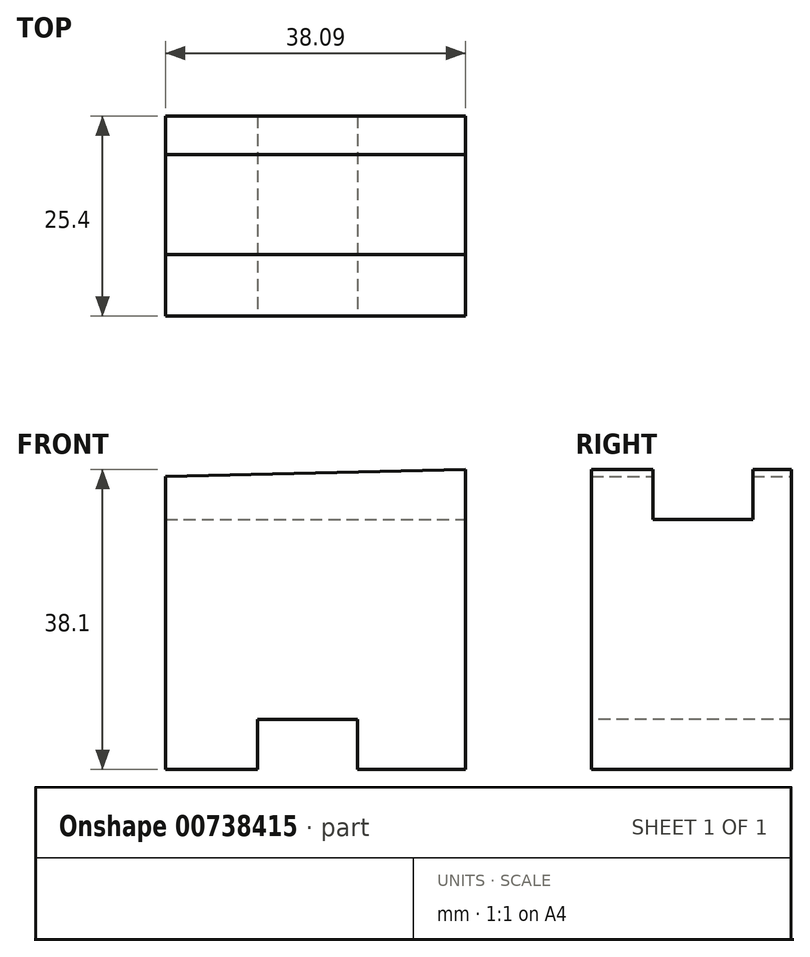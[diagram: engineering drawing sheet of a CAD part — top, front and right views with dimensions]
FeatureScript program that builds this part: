
annotation { "Feature Type Name" : "Feature", "Feature Type Description" : "" }
export const myFeature = defineFeature(function(context is Context, id is Id, definition is map)
    precondition{}
    {
        {
            var Q0;
            Q0=qCreatedBy(makeId("Front.planeOp"),FACE);
            var sketch = newSketch(context, id + "F0", { "sketchPlane" : qUnion([Q0])});
            skLineSegment(sketch, "E0", {"start": v(0, 38.1) * mm, "end": v(0, 0) * mm});
            skLineSegment(sketch, "E1", {"start": v(-0.01, 0.91) * mm, "end": v(38.09, 0.91) * mm});
            skLineSegment(sketch, "E2", {"start": v(38.09, 0.91) * mm, "end": v(38.09, 39.01) * mm});
            skLineSegment(sketch, "E3", {"start": v(38.09, 39.01) * mm, "end": v(0, 38.1) * mm});
            skSolve(sketch);
        }
        {
            var Q0;
            Q0 = qSketchRegion(id + "F0", true);
            extrude(context, id + "F1", {"entities" : qUnion([Q0]), "depth" : 25.4 * mm, "offsetDistance" : 25.4 * mm});
        }
        {
            var Q0;
            Q0=makeQuery(id+"F1.opExtrude","CAP_FACE",FACE,{"disambiguationData":[OSD([sQuery(id+"F0.wireOp",EDGE,"E0"),sQuery(id+"F0.wireOp",EDGE,"E1"),sQuery(id+"F0.wireOp",EDGE,"E2"),sQuery(id+"F0.wireOp",EDGE,"E3")])],"isStart":false});
            var sketch = newSketch(context, id + "F2", { "sketchPlane" : qUnion([Q0])});
            skLineSegment(sketch, "E4", {"start": v(11.67, 7.26) * mm, "end": v(11.67, 0.91) * mm});
            skLineSegment(sketch, "E5", {"start": v(11.67, 7.26) * mm, "end": v(24.37, 7.26) * mm});
            skLineSegment(sketch, "E6", {"start": v(24.37, 7.26) * mm, "end": v(24.37, 0.91) * mm});
            skSolve(sketch);
        }
        {
            var Q0;
            {var subQ0=sQuery(id+"F2.wireOp",EDGE,"E4");Q0=makeQuery(id+"F2.imprint","IMPRINT",FACE,{"disambiguationData":[TD([[makeQuery(id+"F2.imprint","IMPRINT",EDGE,{"derivedFrom":subQ0}),1.0]])]});}
            extrude(context, id + "F3", {"entities" : qUnion([Q0]), "operationType" : NewBodyOperationType.REMOVE, "endBound" : BoundingType.THROUGH_ALL, "oppositeDirection" : true, "depth" : 25.4 * mm, "offsetDistance" : 25.4 * mm});
        }
        {
            var Q0;
            Q0=makeQuery(id+"F1.opExtrude","SWEPT_FACE",FACE,{"disambiguationData":[OSD([sQuery(id+"F0.wireOp",EDGE,"E2")])]});
            var sketch = newSketch(context, id + "F4", { "sketchPlane" : qUnion([Q0])});
            skLineSegment(sketch, "E7", {"start": v(-17.6, 39.01) * mm, "end": v(-17.6, 32.66) * mm});
            skLineSegment(sketch, "E8", {"start": v(-17.6, 32.66) * mm, "end": v(-4.9, 32.66) * mm});
            skLineSegment(sketch, "E9", {"start": v(-4.9, 32.66) * mm, "end": v(-4.9, 39.01) * mm});
            skSolve(sketch);
        }
        {
            var Q0;
            {var subQ0=sQuery(id+"F4.wireOp",EDGE,"E7");Q0=makeQuery(id+"F4.imprint","IMPRINT",FACE,{"disambiguationData":[TD([[makeQuery(id+"F4.imprint","IMPRINT",EDGE,{"derivedFrom":subQ0}),1.0]])]});}
            extrude(context, id + "F5", {"entities" : qUnion([Q0]), "operationType" : NewBodyOperationType.REMOVE, "endBound" : BoundingType.THROUGH_ALL, "oppositeDirection" : true, "depth" : 25.4 * mm, "offsetDistance" : 25.4 * mm});
        }
    });
